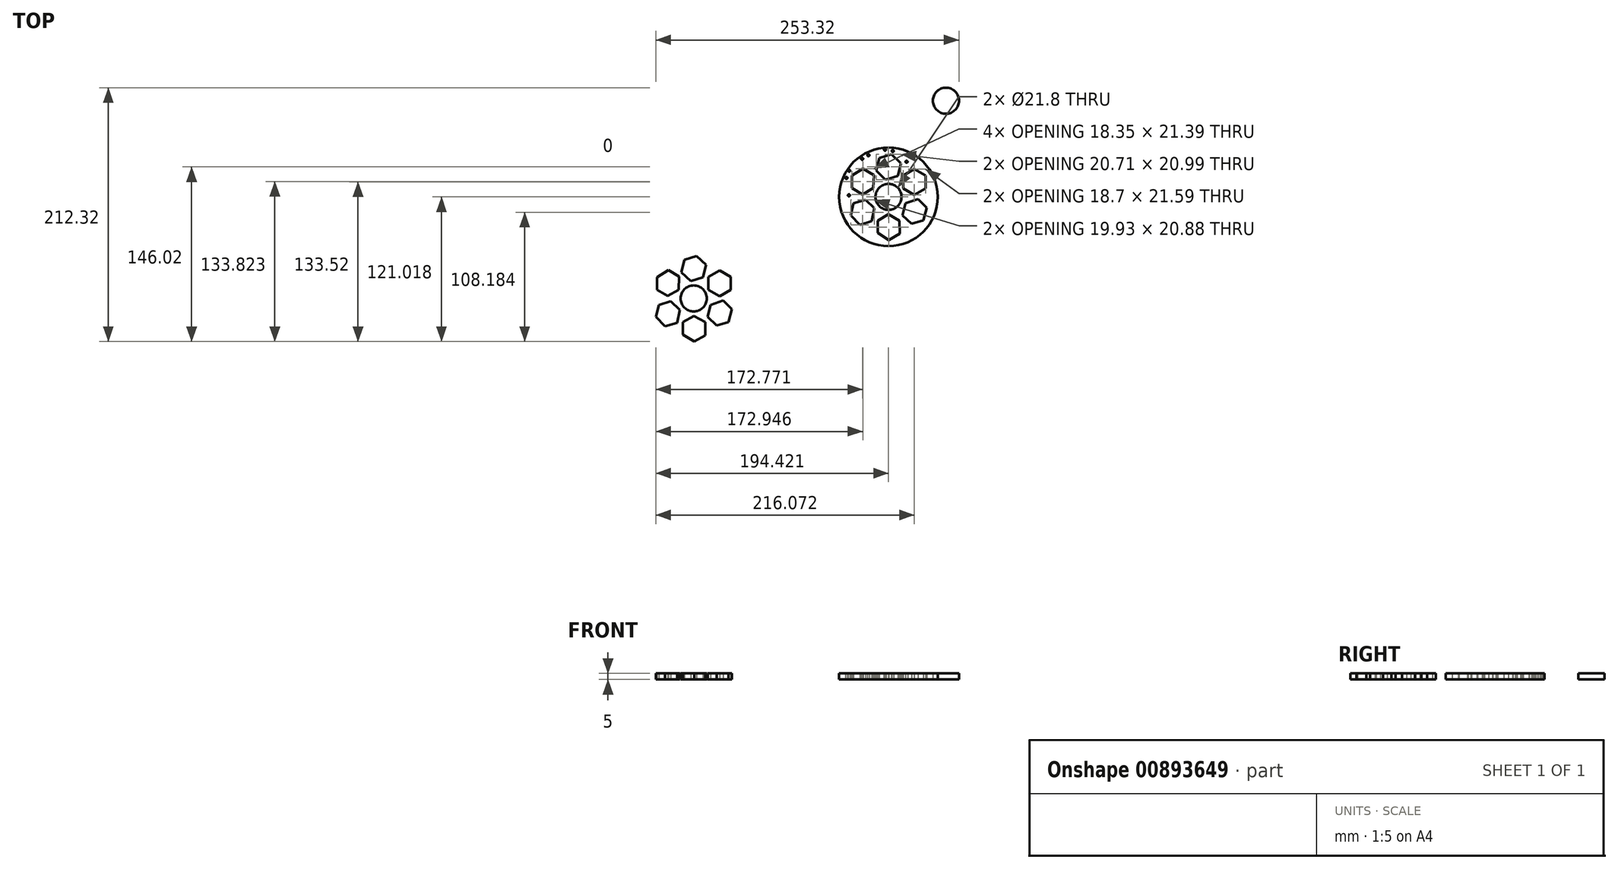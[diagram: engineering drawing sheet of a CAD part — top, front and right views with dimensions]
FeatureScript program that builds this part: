
annotation { "Feature Type Name" : "Feature", "Feature Type Description" : "" }
export const myFeature = defineFeature(function(context is Context, id is Id, definition is map)
    precondition{}
    {
        {
            var Q0;
            Q0=qCreatedBy(makeId("Top.planeOp"),FACE);
            var sketch = newSketch(context, id + "F0", { "sketchPlane" : qUnion([Q0])});
            skCircle(sketch, "E0", {"center": v(599.59, 99.44) * mm, "radius": 10.9 * mm});
            skCircle(sketch, "E1.cCircle", {"center": v(551.6, 44.04) * mm, "radius": 10.8 * mm, "construction": true});
            skLineSegment(sketch, "E1.0", {"start": v(541.24, 40.98) * mm, "end": v(543.76, 51.47) * mm});
            skLineSegment(sketch, "E1.1", {"start": v(543.76, 51.47) * mm, "end": v(554.12, 54.54) * mm});
            skLineSegment(sketch, "E1.2", {"start": v(554.12, 54.54) * mm, "end": v(561.94, 47.1) * mm});
            skLineSegment(sketch, "E1.3", {"start": v(561.94, 47.1) * mm, "end": v(559.42, 36.6) * mm});
            skLineSegment(sketch, "E1.4", {"start": v(559.42, 36.6) * mm, "end": v(549.07, 33.54) * mm});
            skLineSegment(sketch, "E1.5", {"start": v(549.07, 33.54) * mm, "end": v(541.24, 40.98) * mm});
            skLineSegment(sketch, "E2.1.0", {"start": v(539.9, 9.49) * mm, "end": v(537.68, -1.29) * mm});
            skLineSegment(sketch, "E2.1.1", {"start": v(519.98, 3.6) * mm, "end": v(522.4, 13.7) * mm});
            skLineSegment(sketch, "E2.1.2", {"start": v(527.71, -4.24) * mm, "end": v(519.98, 3.6) * mm});
            skLineSegment(sketch, "E2.1.3", {"start": v(522.4, 13.7) * mm, "end": v(532.37, 16.64) * mm});
            skCircle(sketch, "E2.1.4", {"center": v(529.94, 6.54) * mm, "radius": 10.4 * mm, "construction": true});
            skLineSegment(sketch, "E2.1.5", {"start": v(537.68, -1.29) * mm, "end": v(527.71, -4.24) * mm});
            skLineSegment(sketch, "E2.1.6", {"start": v(532.37, 16.64) * mm, "end": v(539.9, 9.49) * mm});
            skLineSegment(sketch, "E2.2.0", {"start": v(565.7, 13.7) * mm, "end": v(576.15, 17.15) * mm});
            skLineSegment(sketch, "E2.2.1", {"start": v(580.78, -0.62) * mm, "end": v(570.81, -3.56) * mm});
            skLineSegment(sketch, "E2.2.2", {"start": v(583.69, 10) * mm, "end": v(580.78, -0.62) * mm});
            skLineSegment(sketch, "E2.2.3", {"start": v(570.81, -3.56) * mm, "end": v(563.28, 3.6) * mm});
            skCircle(sketch, "E2.2.4", {"center": v(573.24, 6.54) * mm, "radius": 10.4 * mm, "construction": true});
            skLineSegment(sketch, "E2.2.5", {"start": v(576.15, 17.15) * mm, "end": v(583.69, 10) * mm});
            skLineSegment(sketch, "E2.2.6", {"start": v(563.28, 3.6) * mm, "end": v(565.7, 13.7) * mm});
            skCircle(sketch, "E3.cCircle", {"center": v(573.24, 31.54) * mm, "radius": 10.8 * mm, "construction": true});
            skLineSegment(sketch, "E3.0", {"start": v(573.24, 42.34) * mm, "end": v(582.6, 36.94) * mm});
            skLineSegment(sketch, "E3.1", {"start": v(582.6, 36.94) * mm, "end": v(582.6, 26.14) * mm});
            skLineSegment(sketch, "E3.2", {"start": v(582.6, 26.14) * mm, "end": v(573.24, 20.74) * mm});
            skLineSegment(sketch, "E3.3", {"start": v(573.24, 20.74) * mm, "end": v(563.9, 26.14) * mm});
            skLineSegment(sketch, "E3.4", {"start": v(563.9, 26.14) * mm, "end": v(563.9, 36.94) * mm});
            skLineSegment(sketch, "E3.5", {"start": v(563.9, 36.94) * mm, "end": v(573.24, 42.34) * mm});
            skCircle(sketch, "E4.1.0", {"center": v(529.94, 31.54) * mm, "radius": 10.4 * mm, "construction": true});
            skLineSegment(sketch, "E4.1.1", {"start": v(538.94, 26.34) * mm, "end": v(529.94, 21.15) * mm});
            skLineSegment(sketch, "E4.1.2", {"start": v(530.3, 42.54) * mm, "end": v(539.3, 37.34) * mm});
            skLineSegment(sketch, "E4.1.3", {"start": v(520.94, 36.74) * mm, "end": v(530.3, 42.54) * mm});
            skLineSegment(sketch, "E4.1.4", {"start": v(529.94, 21.15) * mm, "end": v(520.94, 26.34) * mm});
            skLineSegment(sketch, "E4.1.6", {"start": v(539.3, 37.34) * mm, "end": v(538.94, 26.34) * mm});
            skCircle(sketch, "E4.1.7", {"center": v(551.6, 19.04) * mm, "radius": 10.9 * mm});
            skLineSegment(sketch, "E4.1.8", {"start": v(520.94, 26.34) * mm, "end": v(520.94, 36.74) * mm});
            skCircle(sketch, "E4.2.0", {"center": v(551.6, -5.96) * mm, "radius": 10.4 * mm, "construction": true});
            skLineSegment(sketch, "E4.2.1", {"start": v(551.6, 4.43) * mm, "end": v(560.6, -0.76) * mm});
            skLineSegment(sketch, "E4.2.2", {"start": v(542.6, -11.16) * mm, "end": v(542.6, -0.76) * mm});
            skLineSegment(sketch, "E4.2.3", {"start": v(551.94, -16.96) * mm, "end": v(542.6, -11.16) * mm});
            skLineSegment(sketch, "E4.2.4", {"start": v(560.6, -0.76) * mm, "end": v(560.94, -11.76) * mm});
            skLineSegment(sketch, "E4.2.6", {"start": v(542.6, -0.76) * mm, "end": v(551.6, 4.43) * mm});
            skCircle(sketch, "E4.2.7", {"center": v(551.6, 19.04) * mm, "radius": 10.9 * mm});
            skLineSegment(sketch, "E4.2.8", {"start": v(560.94, -11.76) * mm, "end": v(551.94, -16.96) * mm});
            skLineSegment(sketch, "E5", {"start": v(551.6, 44.04) * mm, "end": v(552.53, 54.07) * mm});
            skLineSegment(sketch, "E6.trimOffspring", {"start": v(550.65, 34.01) * mm, "end": v(551.6, 44.04) * mm});
            skCircle(sketch, "E7", {"center": v(388.79, -65.9) * mm, "radius": 10.9 * mm});
            skCircle(sketch, "E8.cCircle", {"center": v(388.79, -40.9) * mm, "radius": 10.8 * mm, "construction": true});
            skLineSegment(sketch, "E8.0", {"start": v(378.43, -43.96) * mm, "end": v(380.96, -33.46) * mm});
            skLineSegment(sketch, "E8.1", {"start": v(380.96, -33.46) * mm, "end": v(391.3, -30.4) * mm});
            skLineSegment(sketch, "E8.2", {"start": v(391.3, -30.4) * mm, "end": v(399.14, -37.83) * mm});
            skLineSegment(sketch, "E8.3", {"start": v(399.14, -37.83) * mm, "end": v(396.62, -48.33) * mm});
            skLineSegment(sketch, "E8.4", {"start": v(396.62, -48.33) * mm, "end": v(386.26, -51.4) * mm});
            skLineSegment(sketch, "E8.5", {"start": v(386.26, -51.4) * mm, "end": v(378.43, -43.96) * mm});
            skLineSegment(sketch, "E9.1.0", {"start": v(377.1, -75.44) * mm, "end": v(374.87, -86.22) * mm});
            skLineSegment(sketch, "E9.1.1", {"start": v(357.17, -81.34) * mm, "end": v(359.6, -71.24) * mm});
            skLineSegment(sketch, "E9.1.2", {"start": v(364.9, -89.17) * mm, "end": v(357.17, -81.34) * mm});
            skLineSegment(sketch, "E9.1.3", {"start": v(359.6, -71.24) * mm, "end": v(369.56, -68.29) * mm});
            skCircle(sketch, "E9.1.4", {"center": v(367.14, -78.4) * mm, "radius": 10.4 * mm, "construction": true});
            skLineSegment(sketch, "E9.1.5", {"start": v(374.87, -86.22) * mm, "end": v(364.9, -89.17) * mm});
            skLineSegment(sketch, "E9.1.6", {"start": v(369.56, -68.29) * mm, "end": v(377.1, -75.44) * mm});
            skLineSegment(sketch, "E9.2.0", {"start": v(402.9, -71.24) * mm, "end": v(413.42, -67.7) * mm});
            skLineSegment(sketch, "E9.2.1", {"start": v(417.97, -85.55) * mm, "end": v(408, -88.5) * mm});
            skLineSegment(sketch, "E9.2.2", {"start": v(420.57, -74.76) * mm, "end": v(417.97, -85.55) * mm});
            skLineSegment(sketch, "E9.2.3", {"start": v(408, -88.5) * mm, "end": v(400.47, -81.34) * mm});
            skCircle(sketch, "E9.2.4", {"center": v(410.44, -78.4) * mm, "radius": 10.4 * mm, "construction": true});
            skLineSegment(sketch, "E9.2.5", {"start": v(413.42, -67.7) * mm, "end": v(420.57, -74.76) * mm});
            skLineSegment(sketch, "E9.2.6", {"start": v(400.47, -81.34) * mm, "end": v(402.9, -71.24) * mm});
            skCircle(sketch, "E10.cCircle", {"center": v(410.44, -53.4) * mm, "radius": 10.8 * mm, "construction": true});
            skLineSegment(sketch, "E10.0", {"start": v(410.44, -42.6) * mm, "end": v(419.79, -48) * mm});
            skLineSegment(sketch, "E10.1", {"start": v(419.79, -48) * mm, "end": v(419.79, -58.8) * mm});
            skLineSegment(sketch, "E10.2", {"start": v(419.79, -58.8) * mm, "end": v(410.44, -64.19) * mm});
            skLineSegment(sketch, "E10.3", {"start": v(410.44, -64.19) * mm, "end": v(401.09, -58.8) * mm});
            skLineSegment(sketch, "E10.4", {"start": v(401.09, -58.8) * mm, "end": v(401.09, -48) * mm});
            skLineSegment(sketch, "E10.5", {"start": v(401.09, -48) * mm, "end": v(410.44, -42.6) * mm});
            skCircle(sketch, "E11.1.0", {"center": v(367.14, -53.4) * mm, "radius": 10.4 * mm, "construction": true});
            skLineSegment(sketch, "E11.1.1", {"start": v(376.14, -58.59) * mm, "end": v(367.14, -63.79) * mm});
            skLineSegment(sketch, "E11.1.2", {"start": v(367.54, -42.3) * mm, "end": v(376.54, -47.5) * mm});
            skLineSegment(sketch, "E11.1.3", {"start": v(358.14, -48.2) * mm, "end": v(367.54, -42.3) * mm});
            skLineSegment(sketch, "E11.1.4", {"start": v(367.14, -63.79) * mm, "end": v(358.14, -58.59) * mm});
            skLineSegment(sketch, "E11.1.6", {"start": v(376.54, -47.5) * mm, "end": v(376.14, -58.59) * mm});
            skLineSegment(sketch, "E11.1.8", {"start": v(358.14, -58.59) * mm, "end": v(358.14, -48.2) * mm});
            skCircle(sketch, "E11.2.0", {"center": v(388.79, -90.9) * mm, "radius": 10.4 * mm, "construction": true});
            skLineSegment(sketch, "E11.2.1", {"start": v(388.79, -80.5) * mm, "end": v(398.49, -85.7) * mm});
            skLineSegment(sketch, "E11.2.2", {"start": v(379.79, -96.09) * mm, "end": v(379.79, -85.7) * mm});
            skLineSegment(sketch, "E11.2.3", {"start": v(389.19, -101.98) * mm, "end": v(379.79, -96.09) * mm});
            skLineSegment(sketch, "E11.2.4", {"start": v(398.49, -85.7) * mm, "end": v(398.49, -96.79) * mm});
            skLineSegment(sketch, "E11.2.6", {"start": v(379.79, -85.7) * mm, "end": v(388.79, -80.5) * mm});
            skLineSegment(sketch, "E11.2.8", {"start": v(398.49, -96.79) * mm, "end": v(389.19, -101.98) * mm});
            skLineSegment(sketch, "E12", {"start": v(388.79, -40.9) * mm, "end": v(389.73, -30.86) * mm});
            skArc(sketch, "E13", {"start": v(403.42, -40.48) * mm, "mid": v(398.21, -32.2) * mm, "end": v(390.12, -26.68) * mm});
            skArc(sketch, "E14.MirrorCS", {"start": v(374.48, -37.76) * mm, "mid": v(381.15, -30.59) * mm, "end": v(390.12, -26.68) * mm});
            skArc(sketch, "E15.MirrorCS", {"start": v(359.6, -65.9) * mm, "mid": v(355.17, -75.14) * mm, "end": v(355.01, -85.4) * mm});
            skArc(sketch, "E16.MirrorCS", {"start": v(374.2, -91.16) * mm, "mid": v(363.97, -90.38) * mm, "end": v(355.01, -85.4) * mm});
            skArc(sketch, "E17.MirrorCS", {"start": v(403.38, -91.16) * mm, "mid": v(413.6, -90.38) * mm, "end": v(422.56, -85.4) * mm});
            skArc(sketch, "E18.MirrorCS", {"start": v(417.97, -65.9) * mm, "mid": v(422.4, -75.14) * mm, "end": v(422.56, -85.4) * mm});
            skArc(sketch, "E19.MirrorCS", {"start": v(374.37, -39.4) * mm, "mid": v(363.9, -40.7) * mm, "end": v(355.01, -46.4) * mm});
            skArc(sketch, "E20.MirrorCS", {"start": v(359.6, -65.9) * mm, "mid": v(355.17, -56.65) * mm, "end": v(355.01, -46.4) * mm});
            skArc(sketch, "E21.MirrorCS", {"start": v(403.38, -40.62) * mm, "mid": v(413.6, -41.4) * mm, "end": v(422.56, -46.4) * mm});
            skArc(sketch, "E22.MirrorCS", {"start": v(417.97, -65.9) * mm, "mid": v(422.4, -56.65) * mm, "end": v(422.56, -46.4) * mm});
            skArc(sketch, "E23.MirrorCS", {"start": v(403.38, -91.16) * mm, "mid": v(397.59, -99.63) * mm, "end": v(388.79, -104.9) * mm});
            skArc(sketch, "E24.MirrorCS", {"start": v(374.2, -91.16) * mm, "mid": v(379.99, -99.63) * mm, "end": v(388.79, -104.9) * mm});
            skLineSegment(sketch, "E25.trimOffspring", {"start": v(388.79, -51.69) * mm, "end": v(388.79, -40.9) * mm});
            skLineSegment(sketch, "E26", {"start": v(374.37, -39.4) * mm, "end": v(374.48, -37.76) * mm});
            skCircle(sketch, "E27", {"center": v(551.6, 19.04) * mm, "radius": 41.22 * mm});
            skPoint(sketch, "E28.MirrorCS.end.orphan", {"position": v(552.93, 58.25) * mm});
            skPoint(sketch, "E29.start.orphan", {"position": v(510.37, 19.04) * mm});
            skPoint(sketch, "E30.center.orphan", {"position": v(520.94, 21.4) * mm});
            skLineSegment(sketch, "E31", {"start": v(546.1, 28.45) * mm, "end": v(530.83, 54.65) * mm});
            skCircle(sketch, "E32", {"center": v(529.57, 50.87) * mm, "radius": 0.86 * mm});
            skLineSegment(sketch, "E33", {"start": v(520.94, 36.74) * mm, "end": v(515.39, 38.74) * mm});
            skCircle(sketch, "E34.MirrorC", {"center": v(518.67, 41) * mm, "radius": 0.86 * mm});
            skCircle(sketch, "E35.MirrorC", {"center": v(516.46, 34.9) * mm, "radius": 0.86 * mm});
            skCircle(sketch, "E36.MirrorC", {"center": v(518.53, 20.35) * mm, "radius": 0.86 * mm});
            skCircle(sketch, "E37.MirrorC", {"center": v(534.74, 53.89) * mm, "radius": 0.86 * mm});
            skCircle(sketch, "E38.MirrorC", {"center": v(548.7, 58.5) * mm, "radius": 0.86 * mm});
            skCircle(sketch, "E39.MirrorC", {"center": v(555.1, 57.42) * mm, "radius": 0.86 * mm});
            skCircle(sketch, "E40.MirrorC", {"center": v(566.74, 48.45) * mm, "radius": 0.86 * mm});
            skSolve(sketch);
        }
        {
            var Q0;
            Q0 = qSketchRegion(id + "F0", true);
            extrude(context, id + "F1", {"entities" : qUnion([Q0]), "depth" : 5 * mm, "offsetDistance" : 25 * mm});
        }
        {
            var Q0;
            Q0 = qSketchRegion(id + "F0", true);
            extrude(context, id + "F2", {"entities" : qUnion([Q0]), "depth" : 5 * mm, "offsetDistance" : 25 * mm});
        }
    });
